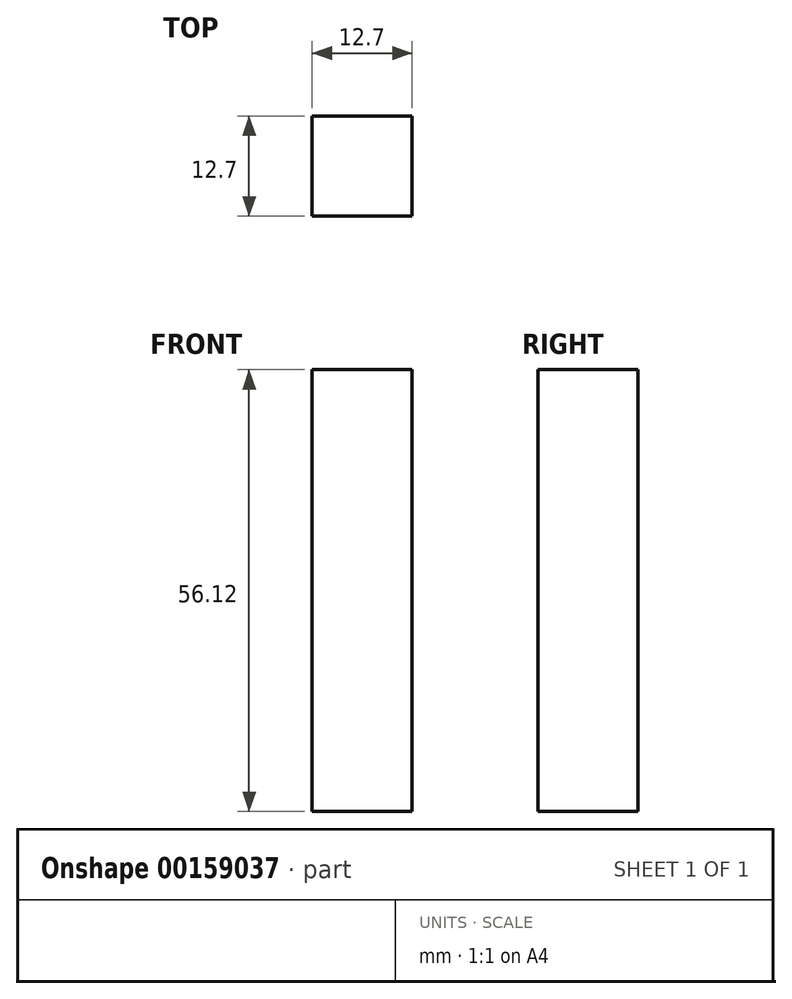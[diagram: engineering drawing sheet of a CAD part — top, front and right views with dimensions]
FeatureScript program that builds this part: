
annotation { "Feature Type Name" : "Feature", "Feature Type Description" : "" }
export const myFeature = defineFeature(function(context is Context, id is Id, definition is map)
    precondition{}
    {
        {
            var Q0;
            Q0=qCreatedBy(makeId("Front.planeOp"),FACE);
            var sketch = newSketch(context, id + "F0", { "sketchPlane" : qUnion([Q0])});
            skLineSegment(sketch, "E0", {"start": v(-7.34, 0) * mm, "end": v(5.36, 0) * mm});
            skLineSegment(sketch, "E1", {"start": v(5.36, 0) * mm, "end": v(5.36, -56.12) * mm});
            skLineSegment(sketch, "E2", {"start": v(5.36, -56.12) * mm, "end": v(-7.34, -56.12) * mm});
            skLineSegment(sketch, "E3", {"start": v(-7.34, -56.12) * mm, "end": v(-7.34, 0) * mm});
            skSolve(sketch);
        }
        {
            var Q0;
            Q0=makeQuery(id+"F0.imprint","IMPRINT",FACE,{"disambiguationData":[TD([[makeQuery(id+"F0.imprint","IMPRINT",EDGE,{"derivedFrom":sQuery(id+"F0.wireOp",EDGE,"E0")}),-1.0]])]});
            extrude(context, id + "F1", {"entities" : qUnion([Q0]), "depth" : 12.7 * mm});
        }
    });
